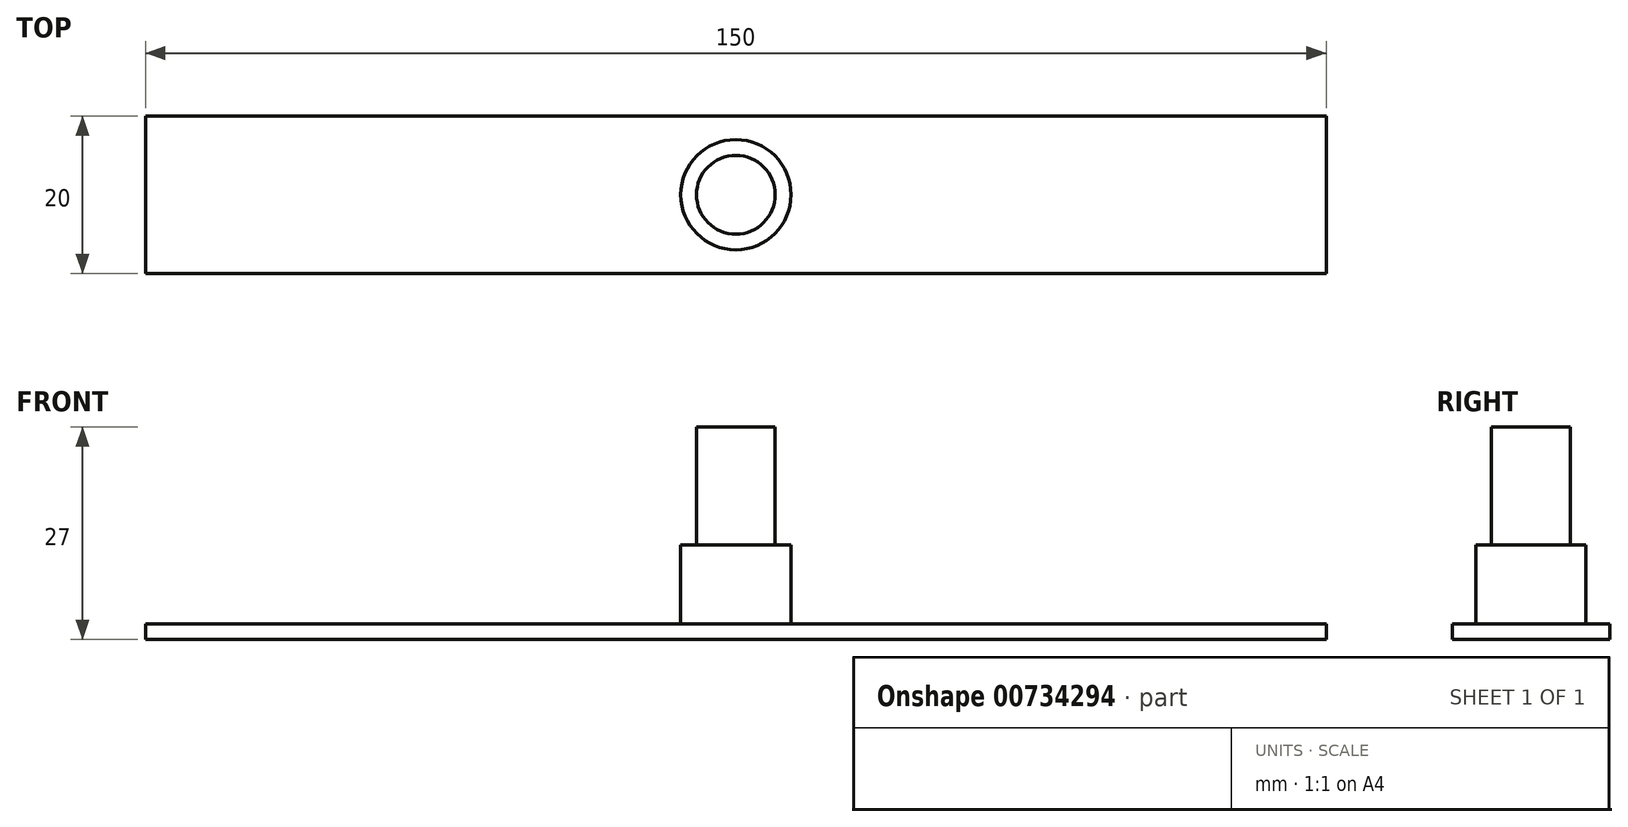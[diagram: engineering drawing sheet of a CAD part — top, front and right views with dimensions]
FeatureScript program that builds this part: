
annotation { "Feature Type Name" : "Feature", "Feature Type Description" : "" }
export const myFeature = defineFeature(function(context is Context, id is Id, definition is map)
    precondition{}
    {
        {
            var Q0;
            Q0=qCreatedBy(makeId("Top.planeOp"),FACE);
            var sketch = newSketch(context, id + "F0", { "sketchPlane" : qUnion([Q0])});
            skLineSegment(sketch, "E0.bottom", {"start": v(75, -10) * mm, "end": v(-75, -10) * mm});
            skLineSegment(sketch, "E0.top", {"start": v(75, 10) * mm, "end": v(-75, 10) * mm});
            skLineSegment(sketch, "E0.left", {"start": v(75, -10) * mm, "end": v(75, 10) * mm});
            skLineSegment(sketch, "E0.right", {"start": v(-75, -10) * mm, "end": v(-75, 10) * mm});
            skPoint(sketch, "E0.middle", {"position": v(0, 0) * mm});
            skSolve(sketch);
        }
        {
            var Q0;
            Q0 = qSketchRegion(id + "F0", true);
            extrude(context, id + "F1", {"entities" : qUnion([Q0]), "depth" : 2 * mm, "offsetDistance" : 25 * mm});
        }
        {
            var Q0;
            Q0=makeQuery(id+"F1.opExtrude","CAP_FACE",FACE,{"disambiguationData":[OSD([sQuery(id+"F0.wireOp",EDGE,"E0.bottom"),sQuery(id+"F0.wireOp",EDGE,"E0.top"),sQuery(id+"F0.wireOp",EDGE,"E0.left"),sQuery(id+"F0.wireOp",EDGE,"E0.right")])],"isStart":false});
            var sketch = newSketch(context, id + "F2", { "sketchPlane" : qUnion([Q0])});
            skCircle(sketch, "E1", {"center": v(0, 0) * mm, "radius": 7 * mm});
            skSolve(sketch);
        }
        {
            var Q0;
            Q0 = qSketchRegion(id + "F2", true);
            extrude(context, id + "F3", {"entities" : qUnion([Q0]), "operationType" : NewBodyOperationType.ADD, "depth" : 25 * mm, "offsetDistance" : 25 * mm});
        }
        {
            var Q0;
            Q0=makeQuery(id+"F3.opExtrude","CAP_FACE",FACE,{"disambiguationData":[OSD([sQuery(id+"F2.wireOp",EDGE,"E1")])],"isStart":false});
            var sketch = newSketch(context, id + "F4", { "sketchPlane" : qUnion([Q0])});
            skCircle(sketch, "E2", {"center": v(0, 0) * mm, "radius": 5 * mm});
            skCircle(sketch, "E3", {"center": v(0, 0) * mm, "radius": 7 * mm});
            skSolve(sketch);
        }
        {
            var Q0;
            Q0 = qSketchRegion(id + "F4", true);
            extrude(context, id + "F5", {"entities" : qUnion([Q0]), "operationType" : NewBodyOperationType.REMOVE, "oppositeDirection" : true, "depth" : 15 * mm, "offsetDistance" : 25 * mm});
        }
    });
